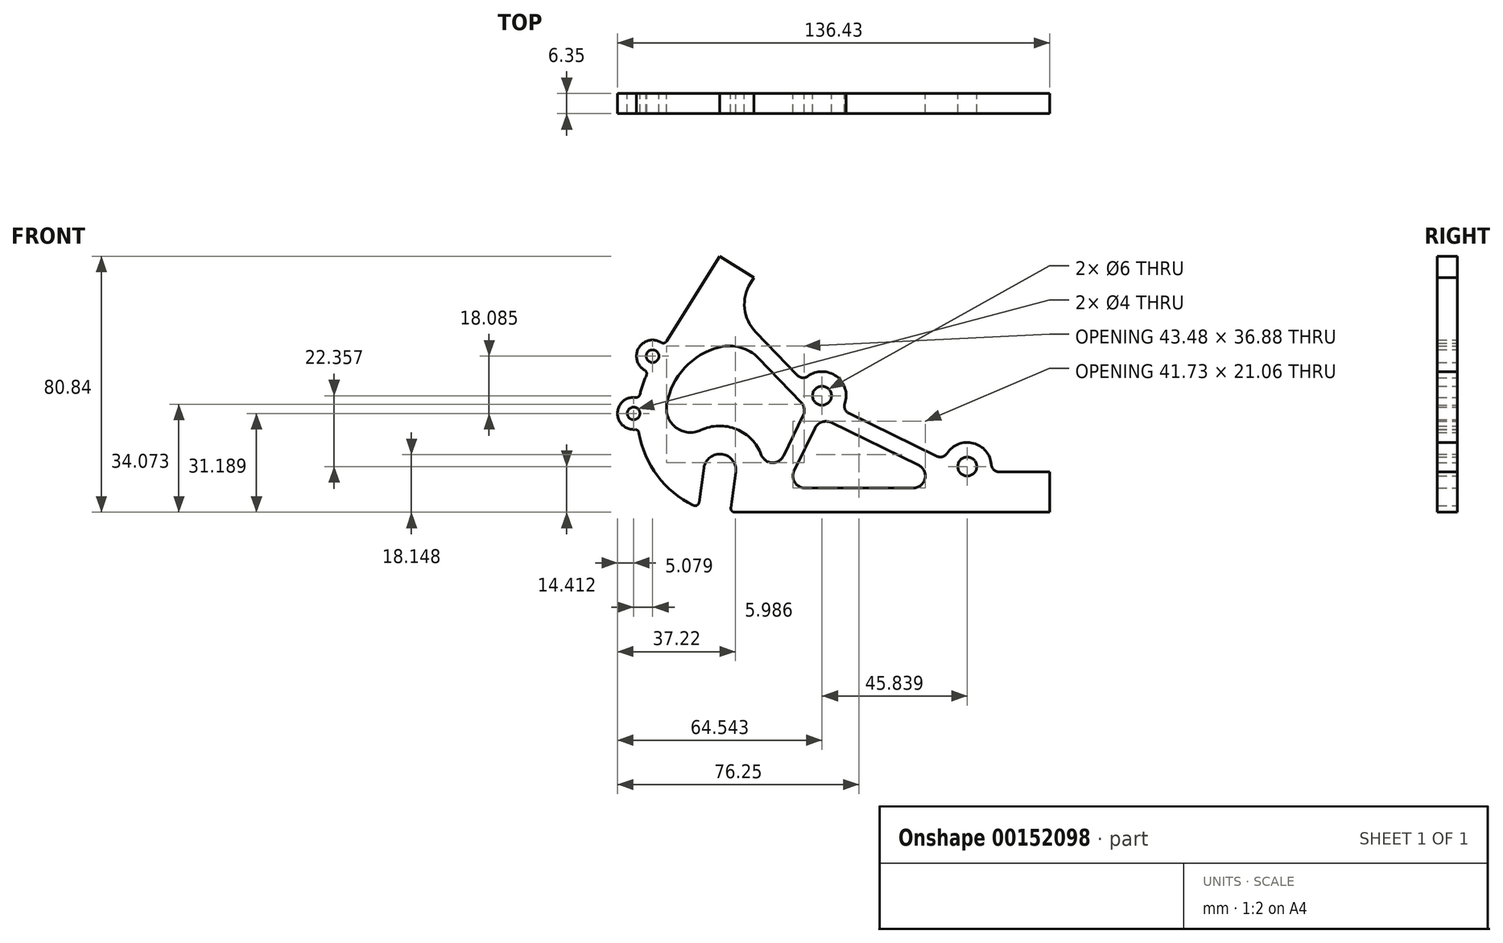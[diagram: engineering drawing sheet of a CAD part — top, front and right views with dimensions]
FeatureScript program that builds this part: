
annotation { "Feature Type Name" : "Feature", "Feature Type Description" : "" }
export const myFeature = defineFeature(function(context is Context, id is Id, definition is map)
    precondition{}
    {
        {
            var Q0;
            Q0=qCreatedBy(makeId("Front.planeOp"),FACE);
            var sketch = newSketch(context, id + "F0", { "sketchPlane" : qUnion([Q0])});
            skCircle(sketch, "E0", {"center": v(0, 0) * mm, "radius": 5.08 * mm, "construction": true});
            skArc(sketch, "E1", {"start": v(-5.03, 0.7) * mm, "mid": v(0.7, 5.03) * mm, "end": v(5.03, -0.7) * mm});
            skLineSegment(sketch, "E2", {"start": v(-5.03, 0.7) * mm, "end": v(-6.56, -10.19) * mm});
            skLineSegment(sketch, "E3", {"start": v(5.03, -0.7) * mm, "end": v(3.47, -11.84) * mm});
            skLineSegment(sketch, "E4", {"start": v(5.03, -0.7) * mm, "end": v(3.26, -13.28) * mm, "construction": true});
            skLineSegment(sketch, "E5", {"start": v(-6.8, -11.87) * mm, "end": v(3.26, -13.28) * mm, "construction": true});
            skArc(sketch, "E6", {"start": v(-6.8, -11.87) * mm, "mid": v(-25.75, 20.58) * mm, "end": v(0, 47.94) * mm, "construction": true});
            skLineSegment(sketch, "E7", {"start": v(0, 0) * mm, "end": v(104.14, 0) * mm, "construction": true});
            skPoint(sketch, "E8", {"position": v(0, 67.56) * mm});
            skLineSegment(sketch, "E9", {"start": v(0, 67.56) * mm, "end": v(-42.22, 0) * mm, "construction": true});
            skLineSegment(sketch, "E10", {"start": v(32.25, 23.49) * mm, "end": v(78.1, 1.13) * mm, "construction": true});
            skLineSegment(sketch, "E11", {"start": v(-27.21, 17.9) * mm, "end": v(-21.22, 36) * mm, "construction": true});
            skLineSegment(sketch, "E12", {"start": v(-27.21, 17.9) * mm, "end": v(-25.94, 17.88) * mm, "construction": true});
            skLineSegment(sketch, "E13", {"start": v(-21.22, 36) * mm, "end": v(-20.15, 35.32) * mm, "construction": true});
            skLineSegment(sketch, "E14", {"start": v(-25.94, 17.88) * mm, "end": v(5.43, 17.03) * mm, "construction": true});
            skCircle(sketch, "E15", {"center": v(-21.22, 36) * mm, "radius": 2 * mm});
            skCircle(sketch, "E16", {"center": v(-27.21, 17.9) * mm, "radius": 2 * mm});
            skCircle(sketch, "E17", {"center": v(32.25, 23.49) * mm, "radius": 3 * mm});
            skCircle(sketch, "E18", {"center": v(78.1, 1.13) * mm, "radius": 3 * mm});
            skArc(sketch, "E19", {"start": v(-13.97, 0) * mm, "mid": v(0, 13.97) * mm, "end": v(13.97, 0) * mm, "construction": true});
            skLineSegment(sketch, "E20", {"start": v(4.72, -13.28) * mm, "end": v(104.14, -13.28) * mm});
            skLineSegment(sketch, "E21", {"start": v(104.14, -13.28) * mm, "end": v(104.14, -0.58) * mm});
            skLineSegment(sketch, "E22", {"start": v(104.14, -0.58) * mm, "end": v(88.22, -0.58) * mm});
            skLineSegment(sketch, "E23", {"start": v(68.47, 4.4) * mm, "end": v(40.76, 17.93) * mm});
            skLineSegment(sketch, "E24", {"start": v(24.48, 29.96) * mm, "end": v(11.33, 43.57) * mm});
            skLineSegment(sketch, "E25", {"start": v(0, 67.56) * mm, "end": v(-16.78, 40.7) * mm});
            skArc(sketch, "E26", {"start": v(-18.53, 40.3) * mm, "mid": v(-25.6, 38.59) * mm, "end": v(-23.71, 31.57) * mm});
            skArc(sketch, "E27", {"start": v(-23.18, 29.94) * mm, "mid": v(-24.33, 26.98) * mm, "end": v(-25.18, 23.93) * mm});
            skArc(sketch, "E28", {"start": v(-26.58, 22.95) * mm, "mid": v(-32.29, 18.05) * mm, "end": v(-26.85, 12.84) * mm});
            skArc(sketch, "E29", {"start": v(-25.51, 11.79) * mm, "mid": v(-19.71, -1.75) * mm, "end": v(-8.38, -11.15) * mm});
            skLineSegment(sketch, "E30", {"start": v(0, 67.56) * mm, "end": v(10.77, 60.83) * mm});
            skLineSegment(sketch, "E31", {"start": v(10.77, 60.83) * mm, "end": v(9.7, 59.12) * mm});
            skArc(sketch, "E32", {"start": v(-16.75, 20.79) * mm, "mid": v(-11.07, 32.32) * mm, "end": v(0, 38.86) * mm});
            skArc(sketch, "E33", {"start": v(-5.97, 12.63) * mm, "mid": v(5.28, 12.93) * mm, "end": v(13.1, 4.84) * mm});
            skArc(sketch, "E34", {"start": v(27.8, 29.67) * mm, "mid": v(36.78, 29.62) * mm, "end": v(39.47, 21.03) * mm});
            skArc(sketch, "E35", {"start": v(71.71, 5.3) * mm, "mid": v(79.97, 8.52) * mm, "end": v(85.69, 1.75) * mm});
            skLineSegment(sketch, "E36", {"start": v(12.2, 35.36) * mm, "end": v(25.6, 21.48) * mm});
            skLineSegment(sketch, "E37", {"start": v(26.29, 17.16) * mm, "end": v(20.1, 4.49) * mm});
            skLineSegment(sketch, "E38", {"start": v(35.13, 15.02) * mm, "end": v(62.7, 1.57) * mm});
            skLineSegment(sketch, "E39", {"start": v(30.04, 13.27) * mm, "end": v(23.48, -0.18) * mm});
            skLineSegment(sketch, "E40", {"start": v(26.9, -5.66) * mm, "end": v(61.04, -5.66) * mm});
            skArc(sketch, "E41", {"start": v(62.7, 1.57) * mm, "mid": v(64.75, -2.71) * mm, "end": v(61.04, -5.66) * mm});
            skLineSegment(sketch, "E42", {"start": v(32.25, 23.49) * mm, "end": v(20.8, 0) * mm, "construction": true});
            skLineSegment(sketch, "E43", {"start": v(27.46, 19.56) * mm, "end": v(29.78, 18.43) * mm, "construction": true});
            skLineSegment(sketch, "E44", {"start": v(29.78, 18.43) * mm, "end": v(31.7, 16.7) * mm, "construction": true});
            skArc(sketch, "E45", {"start": v(13.1, 4.84) * mm, "mid": v(16.49, 2.35) * mm, "end": v(20.1, 4.49) * mm});
            skPoint(sketch, "E46.visualSharp", {"position": v(-13.23, 4.48) * mm});
            skArc(sketch, "E46.filletArc", {"start": v(-16.75, 20.79) * mm, "mid": v(-13.83, 13.44) * mm, "end": v(-5.97, 12.63) * mm});
            skPoint(sketch, "E47.visualSharp", {"position": v(8.36, 39.33) * mm});
            skArc(sketch, "E47.filletArc", {"start": v(12.2, 35.36) * mm, "mid": v(6.57, 38.74) * mm, "end": v(0, 38.86) * mm});
            skPoint(sketch, "E48.visualSharp", {"position": v(27.46, 19.56) * mm});
            skArc(sketch, "E48.filletArc", {"start": v(26.29, 17.16) * mm, "mid": v(26.62, 19.43) * mm, "end": v(25.6, 21.48) * mm});
            skPoint(sketch, "E49.visualSharp", {"position": v(31.7, 16.7) * mm});
            skArc(sketch, "E49.filletArc", {"start": v(35.13, 15.02) * mm, "mid": v(32.22, 15.2) * mm, "end": v(30.04, 13.27) * mm});
            skPoint(sketch, "E50.visualSharp", {"position": v(20.8, -5.66) * mm});
            skArc(sketch, "E50.filletArc", {"start": v(23.48, -0.18) * mm, "mid": v(23.67, -3.87) * mm, "end": v(26.9, -5.66) * mm});
            skPoint(sketch, "E51.visualSharp", {"position": v(4.44, 50.7) * mm});
            skArc(sketch, "E51.filletArc", {"start": v(9.7, 59.12) * mm, "mid": v(7.84, 51.06) * mm, "end": v(11.33, 43.57) * mm});
            skPoint(sketch, "E52.visualSharp", {"position": v(-17.54, 39.5) * mm});
            skArc(sketch, "E52.filletArc", {"start": v(-18.53, 40.3) * mm, "mid": v(-17.57, 40.14) * mm, "end": v(-16.78, 40.7) * mm});
            skPoint(sketch, "E53.visualSharp", {"position": v(-22.62, 31.1) * mm});
            skArc(sketch, "E53.filletArc", {"start": v(-23.18, 29.94) * mm, "mid": v(-23.13, 30.85) * mm, "end": v(-23.71, 31.57) * mm});
            skPoint(sketch, "E54.visualSharp", {"position": v(-25.44, 22.67) * mm});
            skArc(sketch, "E54.filletArc", {"start": v(-26.58, 22.95) * mm, "mid": v(-25.7, 23.17) * mm, "end": v(-25.18, 23.93) * mm});
            skPoint(sketch, "E55.visualSharp", {"position": v(-25.7, 13.06) * mm});
            skArc(sketch, "E55.filletArc", {"start": v(-25.51, 11.79) * mm, "mid": v(-25.98, 12.57) * mm, "end": v(-26.85, 12.84) * mm});
            skPoint(sketch, "E56.visualSharp", {"position": v(26.22, 28.15) * mm});
            skArc(sketch, "E56.filletArc", {"start": v(24.48, 29.96) * mm, "mid": v(26.08, 29.2) * mm, "end": v(27.8, 29.67) * mm});
            skPoint(sketch, "E57.visualSharp", {"position": v(38.45, 19.05) * mm});
            skArc(sketch, "E57.filletArc", {"start": v(39.47, 21.03) * mm, "mid": v(39.53, 19.24) * mm, "end": v(40.76, 17.93) * mm});
            skPoint(sketch, "E58.visualSharp", {"position": v(70.78, 3.28) * mm});
            skArc(sketch, "E58.filletArc", {"start": v(68.47, 4.4) * mm, "mid": v(70.26, 4.24) * mm, "end": v(71.71, 5.3) * mm});
            skPoint(sketch, "E59.visualSharp", {"position": v(70.67, -0.58) * mm});
            skArc(sketch, "E59.filletArc", {"start": v(85.69, 1.75) * mm, "mid": v(86.5, 0.09) * mm, "end": v(88.22, -0.58) * mm});
            skPoint(sketch, "E60.visualSharp", {"position": v(-6.8, -11.87) * mm});
            skArc(sketch, "E60.filletArc", {"start": v(-8.38, -11.15) * mm, "mid": v(-7.22, -11.13) * mm, "end": v(-6.56, -10.19) * mm});
            skPoint(sketch, "E61.visualSharp", {"position": v(3.26, -13.28) * mm});
            skArc(sketch, "E61.filletArc", {"start": v(3.47, -11.84) * mm, "mid": v(3.77, -12.85) * mm, "end": v(4.72, -13.28) * mm});
            skSolve(sketch);
        }
        {
            var Q0;
            Q0 = qSketchRegion(id + "F0", true);
            extrude(context, id + "F1", {"entities" : qUnion([Q0]), "depth" : 6.35 * mm});
        }
    });
